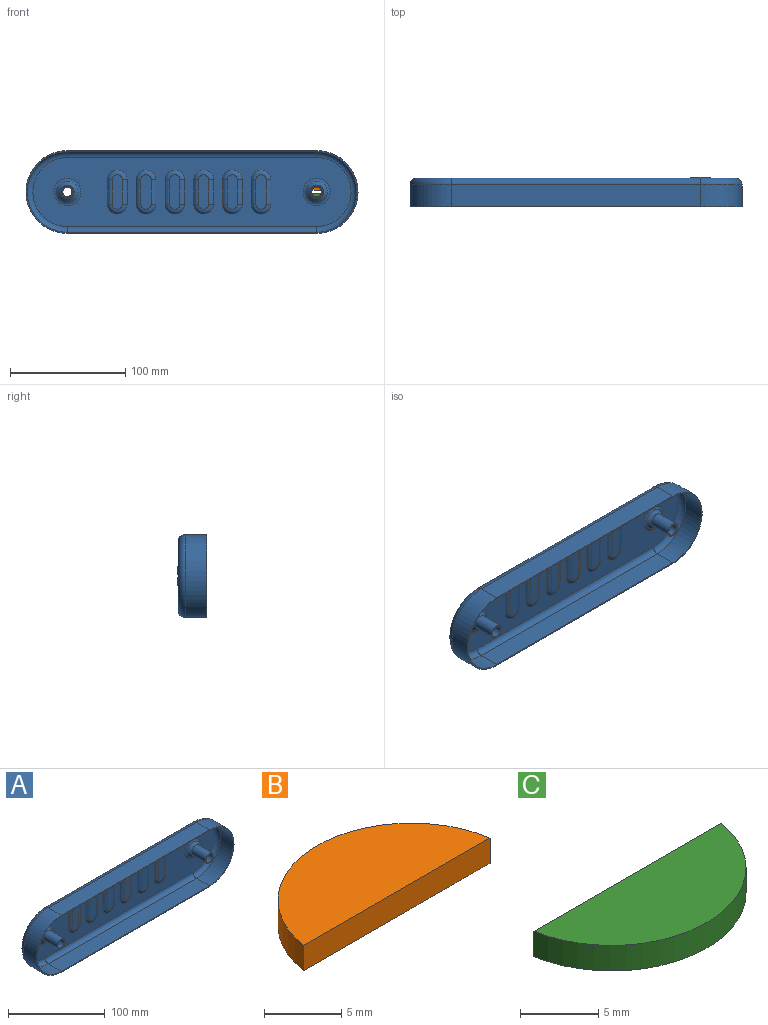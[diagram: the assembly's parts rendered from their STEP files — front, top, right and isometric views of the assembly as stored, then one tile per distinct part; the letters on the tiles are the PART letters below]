
ASSEMBLY  parts=3 mates=2
PART A: 95 faces, bbox 294.6x25x77.9 mm
  f0: plane 12.06x12.06mm, normal (0,-1,0), area 34.7mm2, adj f14,f36
  f1: plane 12.06x12.06mm, normal (0,-1,0), area 34.7mm2, adj f16,f38
  f2: plane 276.66x60mm, normal (0,1,0), area 11997.7mm2, adj f8,f9,f10,f11,f18,f19,f47,f48
  f3: cylinder r=36mm len=72mm, axis (0,1,0), area 2148.7mm2, adj f4,f6,f7,f8
  f4: plane 216.66x19mm, normal (0,0,-1), area 4116.5mm2, adj f3,f5,f7,f10
  f5: cylinder r=36mm len=72mm, axis (0,1,0), area 2148.7mm2, adj f4,f6,f7,f11
  f6: plane 216.66x19mm, normal (0,0,1), area 4116.5mm2, adj f3,f5,f7,f9
  f7: plane 288.66x72mm, normal (0,-1,0), area 656.4mm2, adj f3,f4,f5,f6,f27,f28,f29,f30
  f8: torus R=30mm, axis (0,-1,0), area 1001.3mm2, adj f2,f3,f9,f10
  f9: cylinder r=6mm len=216.66mm, axis (-1,0,0), area 2042mm2, adj f2,f6,f8,f11
  f10: cylinder r=6mm len=216.66mm, axis (1,0,0), area 2042mm2, adj f2,f4,f8,f11
  f11: torus R=30mm, axis (0,-1,0), area 1001.3mm2, adj f2,f5,f9,f10
  f12: cone r=10mm half-angle=50deg, axis (0,1,0), area 236.8mm2, adj f13,f19
  f13: plane 10.06x10.06mm, normal (0,-1,0), area 28.2mm2, adj f12,f14
  f14: cylinder r=5.03mm len=20mm, axis (0,1,0), area 632.1mm2, adj f0,f13
  f15: cone r=10mm half-angle=50deg, axis (0,1,0), area 236.8mm2, adj f17,f18
  f16: cylinder r=5.03mm len=20mm, axis (0,1,0), area 632.1mm2, adj f1,f17
  f17: plane 10.06x10.06mm, normal (0,-1,0), area 28.2mm2, adj f15,f16
  f18: torus R=11.82mm, axis (0,-1,0), area 222.5mm2, adj f2,f15
  f19: torus R=11.82mm, axis (0,-1,0), area 222.5mm2, adj f2,f12
  f20: plane 28x7mm, normal (0,1,0), area 185.5mm2, adj f59,f60,f61,f62
  f21: plane 28x7mm, normal (0,1,0), area 185.5mm2, adj f55,f56,f57,f58
  f22: plane 28x7mm, normal (0,1,0), area 185.5mm2, adj f51,f52,f53,f54
  f23: plane 28x7mm, normal (0,1,0), area 185.5mm2, adj f63,f64,f65,f66
  f24: plane 28x7mm, normal (0,1,0), area 185.5mm2, adj f47,f48,f49,f50
  f25: plane 28x7mm, normal (0,1,0), area 185.5mm2, adj f67,f68,f69,f70
  f26: plane 276.66x60mm, normal (0,-1,0), area 11444.1mm2, adj f31,f32,f33,f34,f39,f40,f71,f72
  f27: cylinder r=35mm len=70mm, axis (0,1,0), area 2089mm2, adj f7,f28,f30,f31
  f28: plane 216.66x19mm, normal (0,0,1), area 4116.5mm2, adj f7,f27,f29,f33
  f29: cylinder r=35mm len=70mm, axis (0,1,0), area 2089mm2, adj f7,f28,f30,f34
  f30: plane 216.66x19mm, normal (0,0,-1), area 4116.5mm2, adj f7,f27,f29,f32
  f31: torus R=30mm, axis (0,-1,0), area 818.7mm2, adj f26,f27,f32,f33
  f32: cylinder r=5mm len=216.66mm, axis (-1,0,0), area 1701.6mm2, adj f26,f30,f31,f34
  f33: cylinder r=5mm len=216.66mm, axis (1,0,0), area 1701.6mm2, adj f26,f28,f31,f34
  f34: torus R=30mm, axis (0,-1,0), area 818.7mm2, adj f26,f29,f32,f33
  f35: cone r=10.64mm half-angle=50deg, axis (0,1,0), area 201.7mm2, adj f36,f40
  f36: cylinder r=6.03mm len=20.43mm, axis (0,1,0), area 771.5mm2, adj f0,f35
  f37: cone r=10.64mm half-angle=50deg, axis (0,1,0), area 201.7mm2, adj f38,f39
  f38: cylinder r=6.03mm len=20.43mm, axis (0,1,0), area 771.5mm2, adj f1,f37
  f39: torus R=11.82mm, axis (0,-1,0), area 183.9mm2, adj f26,f37
  f40: torus R=11.82mm, axis (0,-1,0), area 183.9mm2, adj f26,f35
  f41: plane 30x9mm, normal (0,-1,0), area 252.6mm2, adj f83,f84,f85,f86
  f42: plane 30x9mm, normal (0,-1,0), area 252.6mm2, adj f79,f80,f81,f82
  f43: plane 30x9mm, normal (0,-1,0), area 252.6mm2, adj f75,f76,f77,f78
  f44: plane 30x9mm, normal (0,-1,0), area 252.6mm2, adj f71,f72,f73,f74
  f45: plane 30x9mm, normal (0,-1,0), area 252.6mm2, adj f87,f88,f89,f90
  f46: plane 30x9mm, normal (0,-1,0), area 252.6mm2, adj f91,f92,f93,f94
  f47: torus R=3.5mm, axis (0,-1,0), area 82.4mm2, adj f2,f24,f48,f49
  f48: cylinder r=5mm len=21mm, axis (0,0,-1), area 97.4mm2, adj f2,f24,f47,f50
  f49: cylinder r=5mm len=21mm, axis (0,0,-1), area 97.4mm2, adj f2,f24,f47,f50
  f50: torus R=3.5mm, axis (0,-1,0), area 82.4mm2, adj f2,f24,f48,f49
  f51: torus R=3.5mm, axis (0,-1,0), area 82.4mm2, adj f2,f22,f52,f53
  f52: cylinder r=5mm len=21mm, axis (0,0,-1), area 97.4mm2, adj f2,f22,f51,f54
  f53: cylinder r=5mm len=21mm, axis (0,0,-1), area 97.4mm2, adj f2,f22,f51,f54
  f54: torus R=3.5mm, axis (0,-1,0), area 82.4mm2, adj f2,f22,f52,f53
  f55: torus R=3.5mm, axis (0,-1,0), area 82.4mm2, adj f2,f21,f56,f57
  f56: cylinder r=5mm len=21mm, axis (0,0,-1), area 97.4mm2, adj f2,f21,f55,f58
  f57: cylinder r=5mm len=21mm, axis (0,0,-1), area 97.4mm2, adj f2,f21,f55,f58
  f58: torus R=3.5mm, axis (0,-1,0), area 82.4mm2, adj f2,f21,f56,f57
  f59: torus R=3.5mm, axis (0,-1,0), area 82.4mm2, adj f2,f20,f60,f61
  f60: cylinder r=5mm len=21mm, axis (0,0,-1), area 97.4mm2, adj f2,f20,f59,f62
  f61: cylinder r=5mm len=21mm, axis (0,0,-1), area 97.4mm2, adj f2,f20,f59,f62
  f62: torus R=3.5mm, axis (0,-1,0), area 82.4mm2, adj f2,f20,f60,f61
  f63: torus R=3.5mm, axis (0,-1,0), area 82.4mm2, adj f2,f23,f64,f65
  f64: cylinder r=5mm len=21mm, axis (0,0,-1), area 97.4mm2, adj f2,f23,f63,f66
  f65: cylinder r=5mm len=21mm, axis (0,0,-1), area 97.4mm2, adj f2,f23,f63,f66
  f66: torus R=3.5mm, axis (0,-1,0), area 82.4mm2, adj f2,f23,f64,f65
  f67: torus R=3.5mm, axis (0,-1,0), area 82.4mm2, adj f2,f25,f68,f69
  f68: cylinder r=5mm len=21mm, axis (0,0,-1), area 97.4mm2, adj f2,f25,f67,f70
  f69: cylinder r=5mm len=21mm, axis (0,0,-1), area 97.4mm2, adj f2,f25,f67,f70
  f70: torus R=3.5mm, axis (0,-1,0), area 82.4mm2, adj f2,f25,f68,f69
  f71: cylinder r=5mm len=21mm, axis (0,0,-1), area 97.4mm2, adj f26,f44,f72,f73
  f72: torus R=4.5mm, axis (0,-1,0), area 97mm2, adj f26,f44,f71,f74
  f73: torus R=4.5mm, axis (0,-1,0), area 97mm2, adj f26,f44,f71,f74
  f74: cylinder r=5mm len=21mm, axis (0,0,-1), area 97.4mm2, adj f26,f44,f72,f73
  f75: cylinder r=5mm len=21mm, axis (0,0,-1), area 97.4mm2, adj f26,f43,f76,f77
  f76: torus R=4.5mm, axis (0,-1,0), area 97mm2, adj f26,f43,f75,f78
  f77: torus R=4.5mm, axis (0,-1,0), area 97mm2, adj f26,f43,f75,f78
  f78: cylinder r=5mm len=21mm, axis (0,0,-1), area 97.4mm2, adj f26,f43,f76,f77
  f79: cylinder r=5mm len=21mm, axis (0,0,-1), area 97.4mm2, adj f26,f42,f80,f81
  f80: torus R=4.5mm, axis (0,-1,0), area 97mm2, adj f26,f42,f79,f82
  f81: torus R=4.5mm, axis (0,-1,0), area 97mm2, adj f26,f42,f79,f82
  f82: cylinder r=5mm len=21mm, axis (0,0,-1), area 97.4mm2, adj f26,f42,f80,f81
  f83: torus R=4.5mm, axis (0,-1,0), area 97mm2, adj f26,f41,f84,f85
  f84: cylinder r=5mm len=21mm, axis (0,0,-1), area 97.4mm2, adj f26,f41,f83,f86
  f85: cylinder r=5mm len=21mm, axis (0,0,-1), area 97.4mm2, adj f26,f41,f83,f86
  f86: torus R=4.5mm, axis (0,-1,0), area 97mm2, adj f26,f41,f84,f85
  f87: cylinder r=5mm len=21mm, axis (0,0,-1), area 97.4mm2, adj f26,f45,f88,f89
  f88: torus R=4.5mm, axis (0,-1,0), area 97mm2, adj f26,f45,f87,f90
  f89: torus R=4.5mm, axis (0,-1,0), area 97mm2, adj f26,f45,f87,f90
  f90: cylinder r=5mm len=21mm, axis (0,0,-1), area 97.4mm2, adj f26,f45,f88,f89
  f91: torus R=4.5mm, axis (0,-1,0), area 97mm2, adj f26,f46,f92,f93
  f92: cylinder r=5mm len=21mm, axis (0,0,-1), area 97.4mm2, adj f26,f46,f91,f94
  f93: cylinder r=5mm len=21mm, axis (0,0,-1), area 97.4mm2, adj f26,f46,f91,f94
  f94: torus R=4.5mm, axis (0,-1,0), area 97mm2, adj f26,f46,f92,f93
PART B: 4 faces, bbox 17x7.3x2 mm
  f0: cylinder r=8.61mm len=17.01mm, axis (0,0,-1), area 48.8mm2, adj f1,f2,f3
  f1: plane 17.01x7.29mm, normal (0,0,1), area 93.8mm2, adj f0,f3
  f2: plane 17.01x7.29mm, normal (0,0,-1), area 93.8mm2, adj f0,f3
  f3: plane 17.01x2mm, normal (0,-1,0), area 34mm2, adj f0,f1,f2
PART C: 4 faces, bbox 17x7.2x2 mm
  f0: cylinder r=8.61mm len=16.96mm, axis (0,0,-1), area 48.2mm2, adj f1,f2,f3
  f1: plane 16.96x7.15mm, normal (0,0,-1), area 91.4mm2, adj f0,f3
  f2: plane 16.96x7.15mm, normal (0,0,1), area 91.4mm2, adj f0,f3
  f3: plane 16.96x2mm, normal (0,1,0), area 33.9mm2, adj f0,f1,f2
PLACE A t=(-34.96,-16.44,-13.12)mm
PLACE B rot(axis=(1,0,0),90deg) t=(73.37,-15.61,-13.12)mm
PLACE C rot(axis=(0,0.71,0.71),180deg) t=(73.37,-17.61,-13.12)mm
MATE fastened C.f0 <-> B.f0  axis (0,-1,0) through (73.37,-17.61,-13.12)mm
MATE fastened B.f0 <-> A.f5  axis (0,-1,0) through (73.37,-17.61,-13.12)mm
